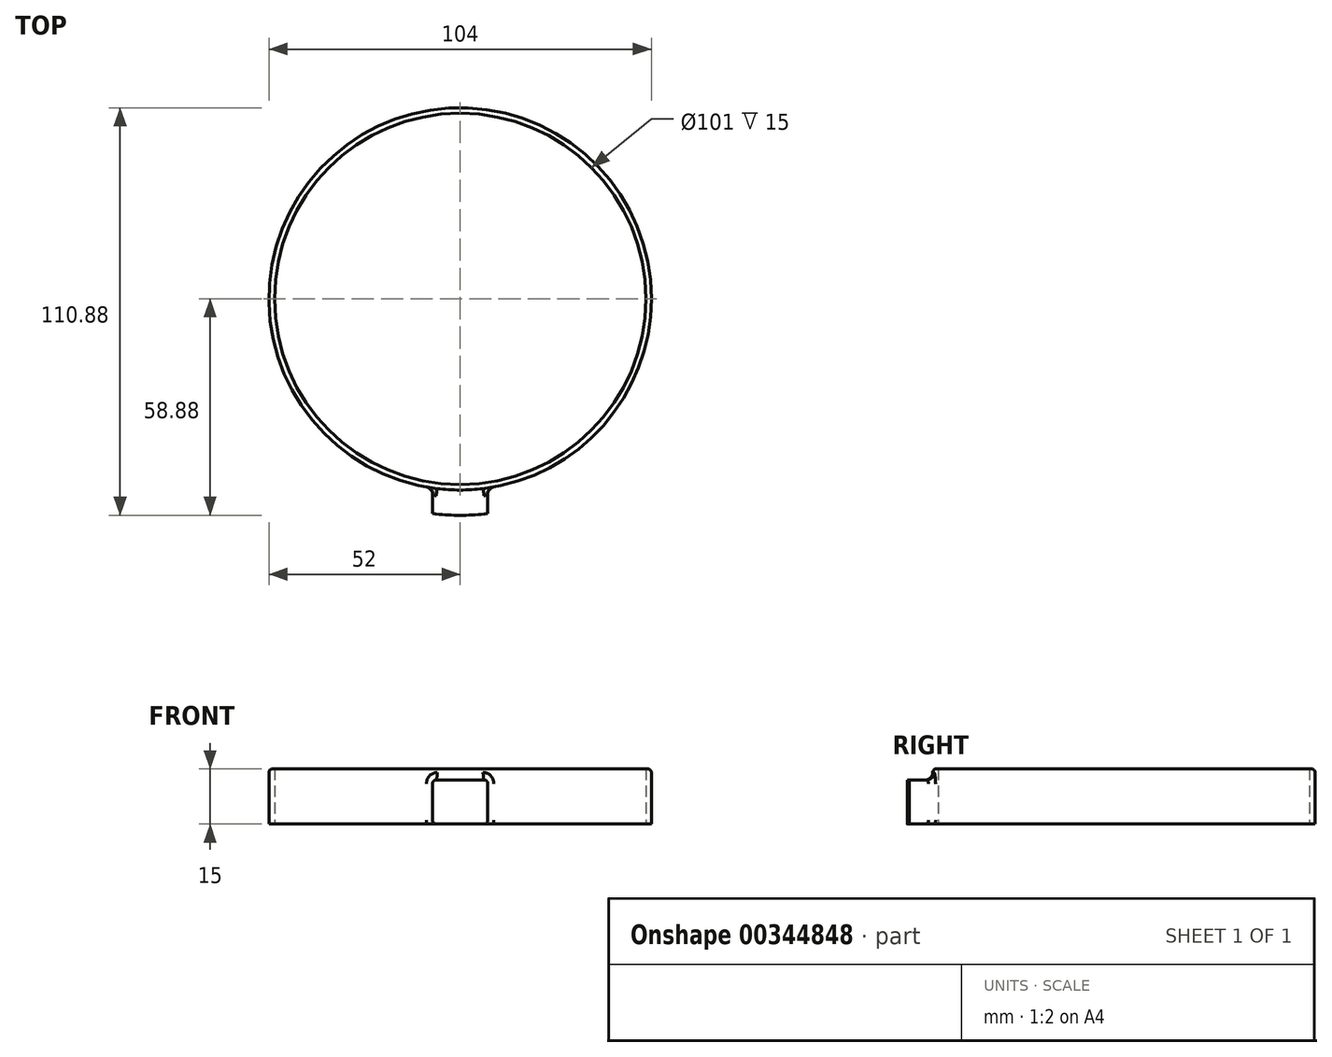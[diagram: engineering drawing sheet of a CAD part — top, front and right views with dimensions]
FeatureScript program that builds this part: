
annotation { "Feature Type Name" : "Feature", "Feature Type Description" : "" }
export const myFeature = defineFeature(function(context is Context, id is Id, definition is map)
    precondition{}
    {
        {
            var Q0;
            Q0=qCreatedBy(makeId("Top.planeOp"),FACE);
            var sketch = newSketch(context, id + "F0", { "sketchPlane" : qUnion([Q0])});
            skCircle(sketch, "E0", {"center": v(0, 0) * mm, "radius": 50.5 * mm});
            skCircle(sketch, "E1", {"center": v(0, 0) * mm, "radius": 52 * mm});
            skSolve(sketch);
        }
        {
            var Q0;
            Q0=makeQuery(id+"F0.imprint","IMPRINT",FACE,{"disambiguationData":[TD([[makeQuery(id+"F0.imprint","IMPRINT",EDGE,{"derivedFrom":sQuery(id+"F0.wireOp",EDGE,"E0")}),-1.0]])]});
            extrude(context, id + "F1", {"entities" : qUnion([Q0]), "depth" : 15 * mm});
        }
        {
            var Q0;
            Q0=qCreatedBy(makeId("Front.planeOp"),FACE);
            cPlane(context, id + "F2", {"entities" : qUnion([Q0]), "cplaneType" : CPlaneType.OFFSET, "offset" : 50.5 * mm, "width" : 150 * mm, "height" : 150 * mm});
        }
        {
            var Q0;
            Q0=qCreatedBy(id+"F2.planeOp",FACE);
            var sketch = newSketch(context, id + "F3", { "sketchPlane" : qUnion([Q0])});
            skLineSegment(sketch, "E2.bottom", {"start": v(7.5, 12) * mm, "end": v(-7.5, 12) * mm});
            skLineSegment(sketch, "E2.top", {"start": v(7.5, 0) * mm, "end": v(-7.5, 0) * mm});
            skLineSegment(sketch, "E2.left", {"start": v(7.5, 12) * mm, "end": v(7.5, 0) * mm});
            skLineSegment(sketch, "E2.right", {"start": v(-7.5, 12) * mm, "end": v(-7.5, 0) * mm});
            skPoint(sketch, "E2.middle", {"position": v(0, 6) * mm});
            skSolve(sketch);
        }
        {
            var Q0;
            Q0 = qSketchRegion(id + "F3", true);
            extrude(context, id + "F4", {"entities" : qUnion([Q0]), "operationType" : NewBodyOperationType.ADD, "depth" : 9 * mm});
        }
        {
            var Q0;
            Q0=makeQuery(id+"F1.opExtrude","CAP_EDGE",EDGE,{"disambiguationData":[OSD([sQuery(id+"F0.wireOp",EDGE,"E1")])],"isStart":false});
            var Q1;
            Q1=makeQuery(id+"F4.opExtrude","SWEPT_EDGE",EDGE,{"disambiguationData":[OSD([sQuery(id+"F3.wireOp",EDGE,"E2.top"),sQuery(id+"F3.wireOp",EDGE,"E2.right")])]});
            var Q2;
            Q2=makeQuery(id+"F4.opExtrude","SWEPT_EDGE",EDGE,{"disambiguationData":[OSD([sQuery(id+"F3.wireOp",EDGE,"E2.bottom"),sQuery(id+"F3.wireOp",EDGE,"E2.right")])]});
            var Q3;
            Q3=makeQuery(id+"F4.opExtrude","SWEPT_EDGE",EDGE,{"disambiguationData":[OSD([sQuery(id+"F3.wireOp",EDGE,"E2.bottom"),sQuery(id+"F3.wireOp",EDGE,"E2.left")])]});
            var Q4;
            Q4=makeQuery(id+"F4.opExtrude","SWEPT_EDGE",EDGE,{"disambiguationData":[OSD([sQuery(id+"F3.wireOp",EDGE,"E2.top"),sQuery(id+"F3.wireOp",EDGE,"E2.left")])]});
            fillet(context, id + "F5", {"entities" : qUnion([Q0, Q1, Q2, Q3, Q4]), "radius" : 1 * mm, "tangentPropagation" : true, "allowEdgeOverflow" : false});
        }
        {
            var Q0;
            Q0=qCreatedBy(makeId("Top.planeOp"),FACE);
            var sketch = newSketch(context, id + "F6", { "sketchPlane" : qUnion([Q0])});
            skArc(sketch, "E3", {"start": v(8.34, -58.29) * mm, "mid": v(0.1, -58.88) * mm, "end": v(-8.14, -58.32) * mm});
            skLineSegment(sketch, "E4", {"start": v(-8.14, -58.32) * mm, "end": v(-8.14, -61.06) * mm});
            skLineSegment(sketch, "E5", {"start": v(-8.14, -61.06) * mm, "end": v(8.34, -61.06) * mm});
            skLineSegment(sketch, "E6", {"start": v(8.34, -61.06) * mm, "end": v(8.34, -58.29) * mm});
            skSolve(sketch);
        }
        {
            var Q0;
            Q0 = qSketchRegion(id + "F6", true);
            extrude(context, id + "F7", {"entities" : qUnion([Q0]), "operationType" : NewBodyOperationType.REMOVE, "depth" : 25 * mm});
        }
        {
            var Q0;
            Q0=makeQuery(id+"F4.boolean.opBoolean","INTERSECT",EDGE,{"derivedFrom":[makeQuery(id+"F1.opExtrude","SWEPT_FACE",FACE,{"disambiguationData":[OSD([sQuery(id+"F0.wireOp",EDGE,"E1")])]}),makeQuery(id+"F4.opExtrude","SWEPT_FACE",FACE,{"disambiguationData":[OSD([sQuery(id+"F3.wireOp",EDGE,"E2.left")])]})]});
            fillet(context, id + "F8", {"entities" : qUnion([Q0]), "radius" : 2 * mm, "tangentPropagation" : true, "allowEdgeOverflow" : false});
        }
    });
